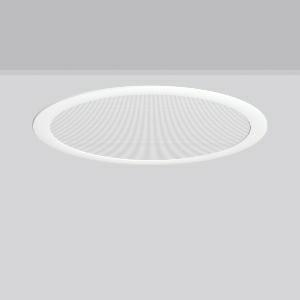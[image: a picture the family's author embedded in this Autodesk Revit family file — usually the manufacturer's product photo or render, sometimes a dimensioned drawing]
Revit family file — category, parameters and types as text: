
# Revit family: toledo_flat_round_e_901669_002_730_393b
name_source: partatom
category: Lighting Fixtures
units: mm (PartAtom-declared; Revit-internal decimal feet)

## family parameters
Cut with Voids When Loaded = No
Host = Face
Light Source = No
Part Type = Normal
Room Calculation Point = No
Round Connector Dimension = Use Diameter
Shared = No

## types (1)
- TuneableWhite 846 (1 x LED Modul 846, 2900 lm, 4600)
    Apparent Load = 30 VA
    CIE Flux Codes = 63 87 96 100 100
    Color Rendering = 80
    Color Temperature = 4600
    Default Elevation = 1800 mm
    Description = Series: TOLEDO FLAT round
Ultra thin recessed downlight. Housing: die-cast aluminium. Lightguide and diffuser made of non-yellowing PMMA, prismatic. Diffuser: transparent plastic, microprismatic. Tunable white dynamically adjustable from 2700 K to 6500 K.With Casambi smart+free Bluetooth control for wireless network and operation using Android / iOS devices, free app available for download. Ceiling installation with spring system. Mounting depth depends on ceiling strength. Including separate LED converter with connecting cable 250 mm. Suitable for through-wiring with separately available accessories. Surface mounted housing as accessory for all sizes. Retrofittable decorative cylinders made of chintz fabric as accessory, optional with satin finish plastic diffuser. Through-wiring box (5 pole) available as accessory. 
Colour: white
Diameter: 495 mm
Height: 6 mm
Cut-out diameter: 470 mm
Recess height: 55-75 mm
Luminaire: recess height: 31-51 mm
Lamp: LED
Socket: without socket
Colour temperature: 2700K - 6500K
Colour rendering index (CRI): 80
System power: 30 W
Rated luminous flux: 2900 lm
Luminous efficiency: 97 lm/W
System power 2: 31 W
Rated luminous flux 2: 2750 lm
Luminous efficiency 2: 89 lm/W
System power 3: 30 W
Rated luminous flux 3: 2800 lm
Luminous efficiency 3: 93 lm/W
Control gear: Dimmable Bluetooth converter
Protection class: II
Type of protection: IP 54
    Height = 0 mm  [stored 0 ft]
    Lamp = 1 x LED Modul 846
    Lamp Light Flux = 2900 lm
    Lamp count = 1
    Length = 495 mm
    Lifetime = 50000 h
    Luminous efficacy = 97 lm/W
    Manufacturer = RZB
    ModVariant = No
    Model = 901669.002.730
    Mounting Place = Ceiling
    Mounting Type = Recessed
    Number of Poles = 1
    OnlyDefault = Yes
    Power Factor = 1
    Product Name = TOLEDO FLAT round E
    Product group = Recessed downlights
    ProductGroupID = 402
    Protection Class = Protection class II
    Protection Degree = IP 20
    RLX_Detail_Level = 1
    RLX_Emergency_Light_Flux = 0 lm
    RLX_Emergency_Type = 0
    RLX_Emergency_Type_DB = No
    RlxData = <blob elided: 104805 chars, md5=90807904>
    Socket = socket
    Standby Power = 0 W
    System Light Flux = 2900 lm
    System Power = 30 W
    Type Comments = TuneableWhite 846
    Type Image = 901586.002.jpg
    URL = http://relux.com
    VarID = tuneablewhite_846
    Voltage = 230 V
    Voltage Range = 220-240 V
    Weight = 0.00 kg
    Width = 0 mm  [stored 0 ft]

note: [stored X ft] marks values corroborated as IEEE doubles in the binary element streams (Revit-internal decimal feet)

## geometry (parser evidence)
native form markers: Blend x4, Sweep x11
no freeform markers — native parametric forms only
